# Revit family: NBS_COBAFlooring_EntMatt_PremierPlusMatting
name_source: partatom
category: Generic Models
revit_build: Autodesk Revit Architecture 2014 (Build: 20140709_2115(x64)
units: mm (PartAtom-declared; Revit-internal decimal feet)

## types (1)
- Premier Plus Matting
    Arrangement = Internally inset in a matwell
    AssetType = Fixed
    BIMObjectName = NBS_COBAFlooring_EntranceMatting_PremierPlusMatting
    BaseColour = Black
    BaseMaterial = 100% recycled PVC
    CarpetColourOptions = Charcoal, Grey
    Combustible = No
    Default Elevation = 1200 mm
    Description = Needlepunch interlinking carpet tiles entrance matting
    Dimensions = 450 x 300 mm
    DurationUnit = year
    EdgingMaterial = NBS_Concept
    EntranceMattingHeight = 18 mm  [stored 0.0590551 ft]
    EntranceMattingMaterial = NBS_COBAFlooring_Carpet_PremierPlusMatting
    Features = Effectively scrapes dirt and wipes moisture, links together to cover all floor sizes, Individual tiles can be moved, cleaned or replaced with ease, flexible and easily cut to shape
    Finish = Carpet strips in a PVC frame
    FireRating = E(F1)
    HasAntiStaticSurface = Yes
    HasNonSkidSurface = No
    IfcExportAs = IfcCoveringType
    IfcExportType = FLOORING
    IntegralAccessories = Edge, Female connector - 300 mm, Female connector - 450 mm, Male connector - 300 mm, Male connector - 450 mm
    ManufacturerName = COBA Flooring
    ManufacturerURL = www.cobaeurope.com
    MattingHeight = 18 mm
    ModelReference = Premier Plus Matting
    NBSCertification = www.nationalbimlibrary.com/cert/b3dduo53
    NBSDescription = Entrance matting
    NBSReference = 45-35-35/420
    Name = EntranceMatting_PremierPlusMatting_COBAFlooring
    Pattern = Horizontal strips (4 per tile)
    ProductInformation = www.cobaeurope.com/entrance-matting-systems/-/datasheets/premier-plus.pdf
    Size = 450 x 300 mm
    SurfaceInsertOptions = Needlepunch PP carpet
    TotalThickness = 0 mm  [stored 0 ft]
    TrafficType = Pedestrian, wheel chairs, pushchairs and trolleys
    Uniclass2 = 45-57-11/426
    Version = 2
    WarrantyDurationParts = 5 years
    WarrantyDurationUnit = year

note: [stored X ft] marks values corroborated as IEEE doubles in the binary element streams (Revit-internal decimal feet)

## geometry (parser evidence)
native form markers: Sweep x1
no freeform markers — native parametric forms only
